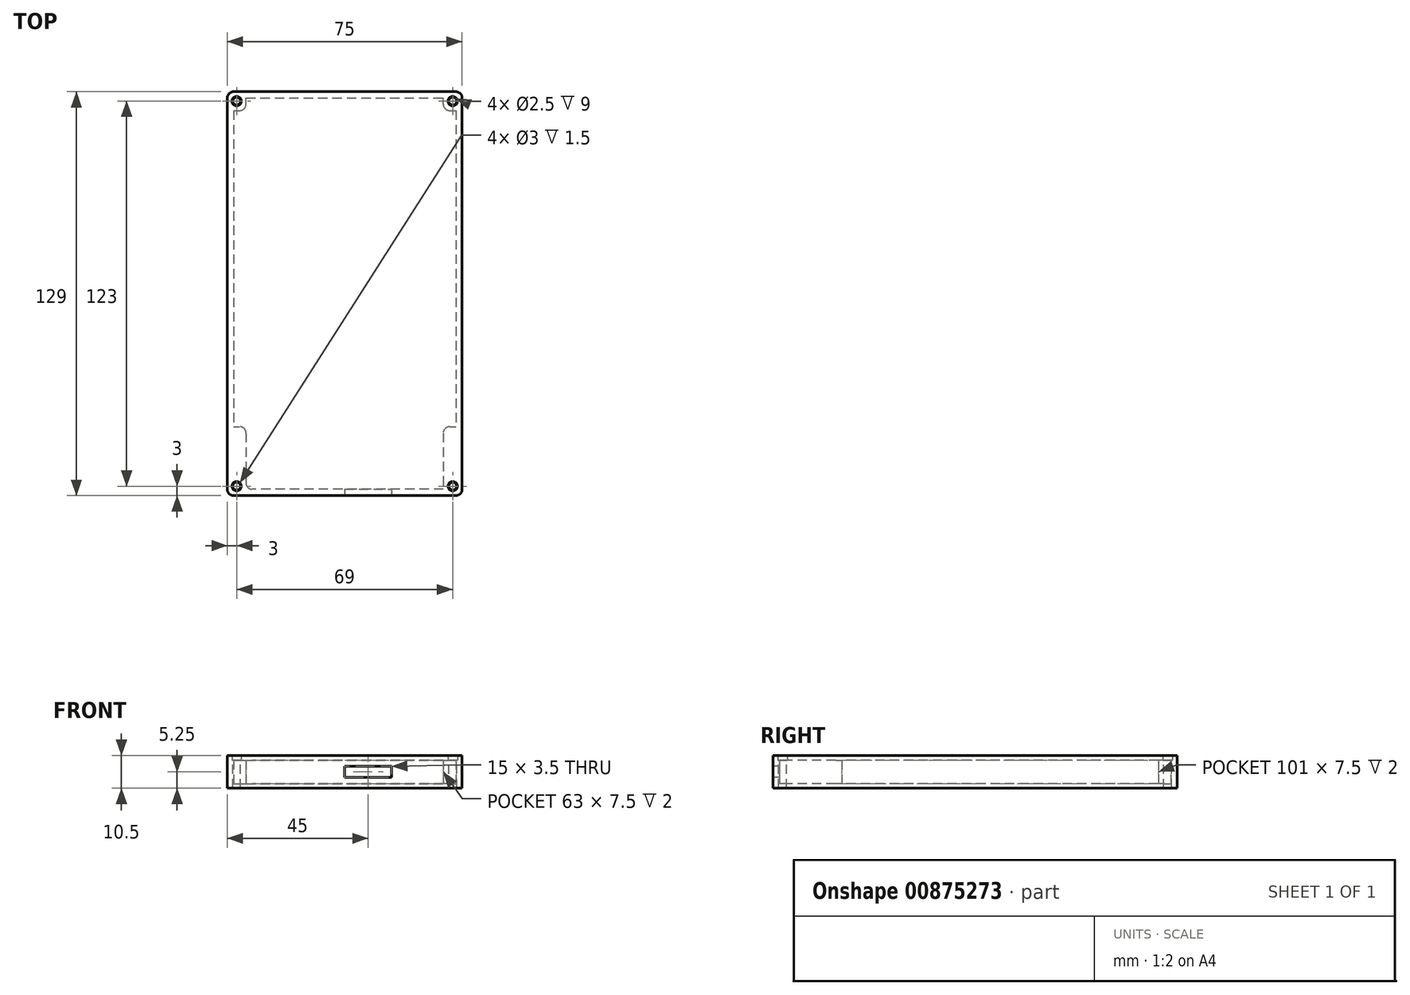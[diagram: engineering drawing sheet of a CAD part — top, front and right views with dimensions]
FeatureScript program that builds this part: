
annotation { "Feature Type Name" : "Feature", "Feature Type Description" : "" }
export const myFeature = defineFeature(function(context is Context, id is Id, definition is map)
    precondition{}
    {
        {
            var Q0;
            Q0=qCreatedBy(makeId("Top.planeOp"),FACE);
            var sketch = newSketch(context, id + "F0", { "sketchPlane" : qUnion([Q0])});
            skLineSegment(sketch, "E0.bottom", {"start": v(-35.5, 50.5) * mm, "end": v(-31.5, 50.5) * mm});
            skLineSegment(sketch, "E0.top", {"start": v(-35.5, -50.5) * mm, "end": v(-31.5, -50.5) * mm});
            skLineSegment(sketch, "E0.left", {"start": v(-35.5, 50.5) * mm, "end": v(-35.5, -50.5) * mm});
            skLineSegment(sketch, "E0.right", {"start": v(35.5, 50.5) * mm, "end": v(35.5, -50.5) * mm});
            skPoint(sketch, "E0.middle", {"position": v(0, 0) * mm});
            skLineSegment(sketch, "E1.bottom", {"start": v(-37.5, 56.5) * mm, "end": v(37.5, 56.5) * mm});
            skLineSegment(sketch, "E1.left", {"start": v(-37.5, 56.5) * mm, "end": v(-37.5, -56.5) * mm});
            skLineSegment(sketch, "E1.right", {"start": v(37.5, 56.5) * mm, "end": v(37.5, -56.5) * mm});
            skLineSegment(sketch, "E2", {"start": v(37.5, -69.5) * mm, "end": v(-37.5, -69.5) * mm, "construction": true});
            skCircle(sketch, "E3", {"center": v(-34.5, -69.5) * mm, "radius": 1.25 * mm});
            skCircle(sketch, "E4", {"center": v(34.5, -69.5) * mm, "radius": 1.25 * mm});
            skLineSegment(sketch, "E5.left", {"start": v(-31.5, -50.5) * mm, "end": v(-31.5, -70.5) * mm});
            skLineSegment(sketch, "E5.right", {"start": v(31.5, -50.5) * mm, "end": v(31.5, -70.5) * mm});
            skLineSegment(sketch, "E6.trimOffspring", {"start": v(31.5, -50.5) * mm, "end": v(35.5, -50.5) * mm});
            skLineSegment(sketch, "E7", {"start": v(37.5, 53.5) * mm, "end": v(-37.5, 53.5) * mm, "construction": true});
            skCircle(sketch, "E8", {"center": v(-34.5, 53.5) * mm, "radius": 1.25 * mm});
            skCircle(sketch, "E9", {"center": v(34.5, 53.5) * mm, "radius": 1.25 * mm});
            skLineSegment(sketch, "E10.top", {"start": v(-31.5, 54.5) * mm, "end": v(31.5, 54.5) * mm});
            skLineSegment(sketch, "E10.left", {"start": v(-31.5, 50.5) * mm, "end": v(-31.5, 54.5) * mm});
            skLineSegment(sketch, "E10.right", {"start": v(31.5, 50.5) * mm, "end": v(31.5, 54.5) * mm});
            skLineSegment(sketch, "E11.trimOffspring", {"start": v(31.5, 50.5) * mm, "end": v(35.5, 50.5) * mm});
            skLineSegment(sketch, "E12", {"start": v(31.5, -70.5) * mm, "end": v(-31.5, -70.5) * mm});
            skLineSegment(sketch, "E13", {"start": v(37.5, -56.5) * mm, "end": v(37.5, -72.5) * mm});
            skLineSegment(sketch, "E14", {"start": v(37.5, -72.5) * mm, "end": v(-37.5, -72.5) * mm});
            skLineSegment(sketch, "E15", {"start": v(-37.5, -72.5) * mm, "end": v(-37.5, -56.5) * mm});
            skLineSegment(sketch, "E16", {"start": v(15, -70.5) * mm, "end": v(15, -72.5) * mm});
            skLineSegment(sketch, "E17", {"start": v(0, -70.5) * mm, "end": v(0, -72.5) * mm});
            skSolve(sketch);
        }
        {
            var Q0;
            {var subQ4=sQuery(id+"F0.wireOp",EDGE,"E0.bottom");Q0=makeQuery(id+"F0.imprint","IMPRINT",FACE,{"disambiguationData":[TD([[makeQuery(id+"F0.imprint","IMPRINT",EDGE,{"derivedFrom":subQ4}),1.0]])]});}
            var Q1;
            {var subQ3=sQuery(id+"F0.wireOp",EDGE,"E0.bottom");Q1=makeQuery(id+"F0.imprint","IMPRINT",FACE,{"disambiguationData":[TD([[makeQuery(id+"F0.imprint","IMPRINT",EDGE,{"derivedFrom":subQ3}),-1.0]])]});}
            var Q2;
            {var subQ0=sQuery(id+"F0.wireOp",EDGE,"0kvsNTW8-W47e-l9aU-NlA9-IWJdQwKUpimK");Q2=makeQuery(id+"F0.imprint","IMPRINT",FACE,{"disambiguationData":[TD([[makeQuery(id+"F0.imprint","IMPRINT",EDGE,{"derivedFrom":subQ0}),-1.0]])]});}
            var Q3;
            {var subQ2=sQuery(id+"F0.wireOp",EDGE,"E16");Q3=makeQuery(id+"F0.imprint","IMPRINT",FACE,{"disambiguationData":[TD([[makeQuery(id+"F0.imprint","IMPRINT",EDGE,{"derivedFrom":subQ2}),-1.0]])]});}
            extrude(context, id + "F1", {"entities" : qUnion([Q0, Q1, Q2, Q3]), "depth" : -1.5 * mm, "offsetDistance" : 25 * mm});
        }
        {
            var Q0;
            {var subQ4=sQuery(id+"F0.wireOp",EDGE,"E0.bottom");Q0=makeQuery(id+"F0.imprint","IMPRINT",FACE,{"disambiguationData":[TD([[makeQuery(id+"F0.imprint","IMPRINT",EDGE,{"derivedFrom":subQ4}),1.0]])]});}
            extrude(context, id + "F2", {"entities" : qUnion([Q0]), "operationType" : NewBodyOperationType.ADD, "depth" : 7.5 * mm, "offsetDistance" : 25 * mm});
        }
        {
            var Q0;
            {var subQ0=sQuery(id+"F0.wireOp",EDGE,"E1.right");var subQ1=sQuery(id+"F0.wireOp",EDGE,"E1.top");Q0=makeQuery(id+"F2.boolean.opBoolean","MERGE",EDGE,{"derivedFrom":[makeQuery(id+"F1.opExtrude","SWEPT_EDGE",EDGE,{"disambiguationData":[OSD([subQ1,subQ0])]}),makeQuery(id+"F2.opExtrude","SWEPT_EDGE",EDGE,{"disambiguationData":[OSD([subQ1,subQ0])]})]});}
            var Q1;
            {var subQ0=sQuery(id+"F0.wireOp",EDGE,"E1.right");var subQ1=sQuery(id+"F0.wireOp",EDGE,"E1.bottom");Q1=makeQuery(id+"F2.boolean.opBoolean","MERGE",EDGE,{"derivedFrom":[makeQuery(id+"F1.opExtrude","SWEPT_EDGE",EDGE,{"disambiguationData":[OSD([subQ1,subQ0])]}),makeQuery(id+"F2.opExtrude","SWEPT_EDGE",EDGE,{"disambiguationData":[OSD([subQ1,subQ0])]})]});}
            var Q2;
            {var subQ0=sQuery(id+"F0.wireOp",EDGE,"E1.left");var subQ1=sQuery(id+"F0.wireOp",EDGE,"E1.bottom");Q2=makeQuery(id+"F2.boolean.opBoolean","MERGE",EDGE,{"derivedFrom":[makeQuery(id+"F1.opExtrude","SWEPT_EDGE",EDGE,{"disambiguationData":[OSD([subQ1,subQ0])]}),makeQuery(id+"F2.opExtrude","SWEPT_EDGE",EDGE,{"disambiguationData":[OSD([subQ1,subQ0])]})]});}
            var Q3;
            Q3=makeQuery(id+"F2.opExtrude","SWEPT_EDGE",EDGE,{"disambiguationData":[OSD([sQuery(id+"F0.wireOp",EDGE,"E5.right"),sQuery(id+"F0.wireOp",EDGE,"E6.trimOffspring")])]});
            var Q4;
            Q4=makeQuery(id+"F2.opExtrude","SWEPT_EDGE",EDGE,{"disambiguationData":[OSD([sQuery(id+"F0.wireOp",EDGE,"E5.top"),sQuery(id+"F0.wireOp",EDGE,"E5.left")])]});
            var Q5;
            {var subQ0=sQuery(id+"F0.wireOp",EDGE,"E1.left");var subQ1=sQuery(id+"F0.wireOp",EDGE,"E1.top");Q5=makeQuery(id+"F2.boolean.opBoolean","MERGE",EDGE,{"derivedFrom":[makeQuery(id+"F1.opExtrude","SWEPT_EDGE",EDGE,{"disambiguationData":[OSD([subQ1,subQ0])]}),makeQuery(id+"F2.opExtrude","SWEPT_EDGE",EDGE,{"disambiguationData":[OSD([subQ1,subQ0])]})]});}
            var Q6;
            Q6=makeQuery(id+"F2.opExtrude","SWEPT_EDGE",EDGE,{"disambiguationData":[OSD([sQuery(id+"F0.wireOp",EDGE,"E0.bottom"),sQuery(id+"F0.wireOp",EDGE,"E10.left")])]});
            var Q7;
            Q7=makeQuery(id+"F2.opExtrude","SWEPT_EDGE",EDGE,{"disambiguationData":[OSD([sQuery(id+"F0.wireOp",EDGE,"E10.right"),sQuery(id+"F0.wireOp",EDGE,"E11.trimOffspring")])]});
            var Q8;
            Q8=makeQuery(id+"F2.opExtrude","SWEPT_EDGE",EDGE,{"disambiguationData":[OSD([sQuery(id+"F0.wireOp",EDGE,"E0.top"),sQuery(id+"F0.wireOp",EDGE,"E5.left")])]});
            var Q9;
            {var subQ0=sQuery(id+"F0.wireOp",EDGE,"E14");var subQ1=sQuery(id+"F0.wireOp",EDGE,"E13");Q9=makeQuery(id+"F2.boolean.opBoolean","MERGE",EDGE,{"derivedFrom":[makeQuery(id+"F1.opExtrude","SWEPT_EDGE",EDGE,{"disambiguationData":[OSD([subQ1,subQ0])]}),makeQuery(id+"F2.opExtrude","SWEPT_EDGE",EDGE,{"disambiguationData":[OSD([subQ1,subQ0])]})]});}
            var Q10;
            {var subQ0=sQuery(id+"F0.wireOp",EDGE,"E15");var subQ1=sQuery(id+"F0.wireOp",EDGE,"E14");Q10=makeQuery(id+"F2.boolean.opBoolean","MERGE",EDGE,{"derivedFrom":[makeQuery(id+"F1.opExtrude","SWEPT_EDGE",EDGE,{"disambiguationData":[OSD([subQ1,subQ0])]}),makeQuery(id+"F2.opExtrude","SWEPT_EDGE",EDGE,{"disambiguationData":[OSD([subQ1,subQ0])]})]});}
            fillet(context, id + "F3", {"entities" : qUnion([Q0, Q1, Q2, Q3, Q4, Q5, Q6, Q7, Q8, Q9, Q10]), "tangentPropagation" : true, "radius" : 2 * mm, "defaultsChanged" : false, "vertexSettings" : [], "allowEdgeOverflow" : false});
        }
        {
            var Q0;
            {var subQ2=sQuery(id+"F0.wireOp",EDGE,"E16");Q0=makeQuery(id+"F0.imprint","IMPRINT",FACE,{"disambiguationData":[TD([[makeQuery(id+"F0.imprint","IMPRINT",EDGE,{"derivedFrom":subQ2}),-1.0]])]});}
            extrude(context, id + "F4", {"entities" : qUnion([Q0]), "operationType" : NewBodyOperationType.ADD, "surfaceOperationType" : NewSurfaceOperationType.ADD, "depth" : 2 * mm, "offsetDistance" : 25 * mm});
        }
        {
            var Q0;
            Q0=makeQuery(id+"F2.opExtrude","CAP_FACE",FACE,{"disambiguationData":[OSD([sQuery(id+"F0.wireOp",EDGE,"E0.bottom"),sQuery(id+"F0.wireOp",EDGE,"E0.top"),sQuery(id+"F0.wireOp",EDGE,"E0.left"),sQuery(id+"F0.wireOp",EDGE,"E0.right"),sQuery(id+"F0.wireOp",EDGE,"E1.bottom"),sQuery(id+"F0.wireOp",EDGE,"E1.left"),sQuery(id+"F0.wireOp",EDGE,"E1.right"),sQuery(id+"F0.wireOp",EDGE,"E3"),sQuery(id+"F0.wireOp",EDGE,"E4"),sQuery(id+"F0.wireOp",EDGE,"E5.left"),sQuery(id+"F0.wireOp",EDGE,"E5.right"),sQuery(id+"F0.wireOp",EDGE,"E6.trimOffspring"),sQuery(id+"F0.wireOp",EDGE,"E8"),sQuery(id+"F0.wireOp",EDGE,"E9"),sQuery(id+"F0.wireOp",EDGE,"E10.top"),sQuery(id+"F0.wireOp",EDGE,"E10.left"),sQuery(id+"F0.wireOp",EDGE,"E10.right"),sQuery(id+"F0.wireOp",EDGE,"E11.trimOffspring"),sQuery(id+"F0.wireOp",EDGE,"E12"),sQuery(id+"F0.wireOp",EDGE,"E13"),sQuery(id+"F0.wireOp",EDGE,"E14"),sQuery(id+"F0.wireOp",EDGE,"E15"),sQuery(id+"F0.wireOp",EDGE,"E16"),sQuery(id+"F0.wireOp",EDGE,"E17")])],"isStart":false});
            var sketch = newSketch(context, id + "F5", { "sketchPlane" : qUnion([Q0])});
            skPoint(sketch, "E18.firstSnap0", {"position": v(36.91, 56.5) * mm});
            skLineSegment(sketch, "E18.bottom", {"start": v(37.5, 56.5) * mm, "end": v(-37.5, 56.5) * mm});
            skLineSegment(sketch, "E18.top", {"start": v(37.5, -72.5) * mm, "end": v(-37.5, -72.5) * mm});
            skLineSegment(sketch, "E18.left", {"start": v(37.5, 56.5) * mm, "end": v(37.5, -72.5) * mm});
            skLineSegment(sketch, "E18.right", {"start": v(-37.5, 56.5) * mm, "end": v(-37.5, -72.5) * mm});
            skCircle(sketch, "E19", {"center": v(-34.5, 53.5) * mm, "radius": 1.5 * mm});
            skCircle(sketch, "E20", {"center": v(34.5, 53.5) * mm, "radius": 1.5 * mm});
            skCircle(sketch, "E21", {"center": v(34.5, -69.5) * mm, "radius": 1.5 * mm});
            skCircle(sketch, "E22", {"center": v(-34.5, -69.5) * mm, "radius": 1.5 * mm});
            skLineSegment(sketch, "E23.bottom", {"start": v(0, -72.5) * mm, "end": v(15, -72.5) * mm});
            skLineSegment(sketch, "E23.top", {"start": v(0, -70.5) * mm, "end": v(15, -70.5) * mm});
            skLineSegment(sketch, "E23.left", {"start": v(0, -72.5) * mm, "end": v(0, -70.5) * mm});
            skLineSegment(sketch, "E23.right", {"start": v(15, -72.5) * mm, "end": v(15, -70.5) * mm});
            skSolve(sketch);
        }
        {
            var Q0;
            Q0 = qSketchRegion(id + "F5", true);
            extrude(context, id + "F6", {"entities" : qUnion([Q0]), "depth" : 1.5 * mm, "offsetDistance" : 25 * mm});
        }
        {
            var Q0;
            Q0=makeQuery(id+"F6.opExtrude","SWEPT_EDGE",EDGE,{"disambiguationData":[OSD([sQuery(id+"F5.wireOp",EDGE,"E18.bottom"),sQuery(id+"F5.wireOp",EDGE,"E18.right")])]});
            var Q1;
            Q1=makeQuery(id+"F6.opExtrude","SWEPT_EDGE",EDGE,{"disambiguationData":[OSD([sQuery(id+"F5.wireOp",EDGE,"E18.bottom"),sQuery(id+"F5.wireOp",EDGE,"E18.left")])]});
            var Q2;
            Q2=makeQuery(id+"F6.opExtrude","SWEPT_EDGE",EDGE,{"disambiguationData":[OSD([sQuery(id+"F5.wireOp",EDGE,"E18.top"),sQuery(id+"F5.wireOp",EDGE,"E18.right")])]});
            var Q3;
            Q3=makeQuery(id+"F6.opExtrude","SWEPT_EDGE",EDGE,{"disambiguationData":[OSD([sQuery(id+"F5.wireOp",EDGE,"E18.top"),sQuery(id+"F5.wireOp",EDGE,"E18.left")])]});
            fillet(context, id + "F7", {"entities" : qUnion([Q0, Q1, Q2, Q3]), "tangentPropagation" : true, "radius" : 2 * mm, "defaultsChanged" : false, "vertexSettings" : [], "allowEdgeOverflow" : false});
        }
        {
            var Q0;
            Q0=makeQuery(id+"F5.imprint","IMPRINT",FACE,{"disambiguationData":[TD([[makeQuery(id+"F5.imprint","IMPRINT",EDGE,{"derivedFrom":sQuery(id+"F5.wireOp",EDGE,"E23.top")}),-1.0]])]});
            extrude(context, id + "F8", {"entities" : qUnion([Q0]), "operationType" : NewBodyOperationType.ADD, "oppositeDirection" : true, "depth" : 2 * mm, "offsetDistance" : 25 * mm});
        }
    });
